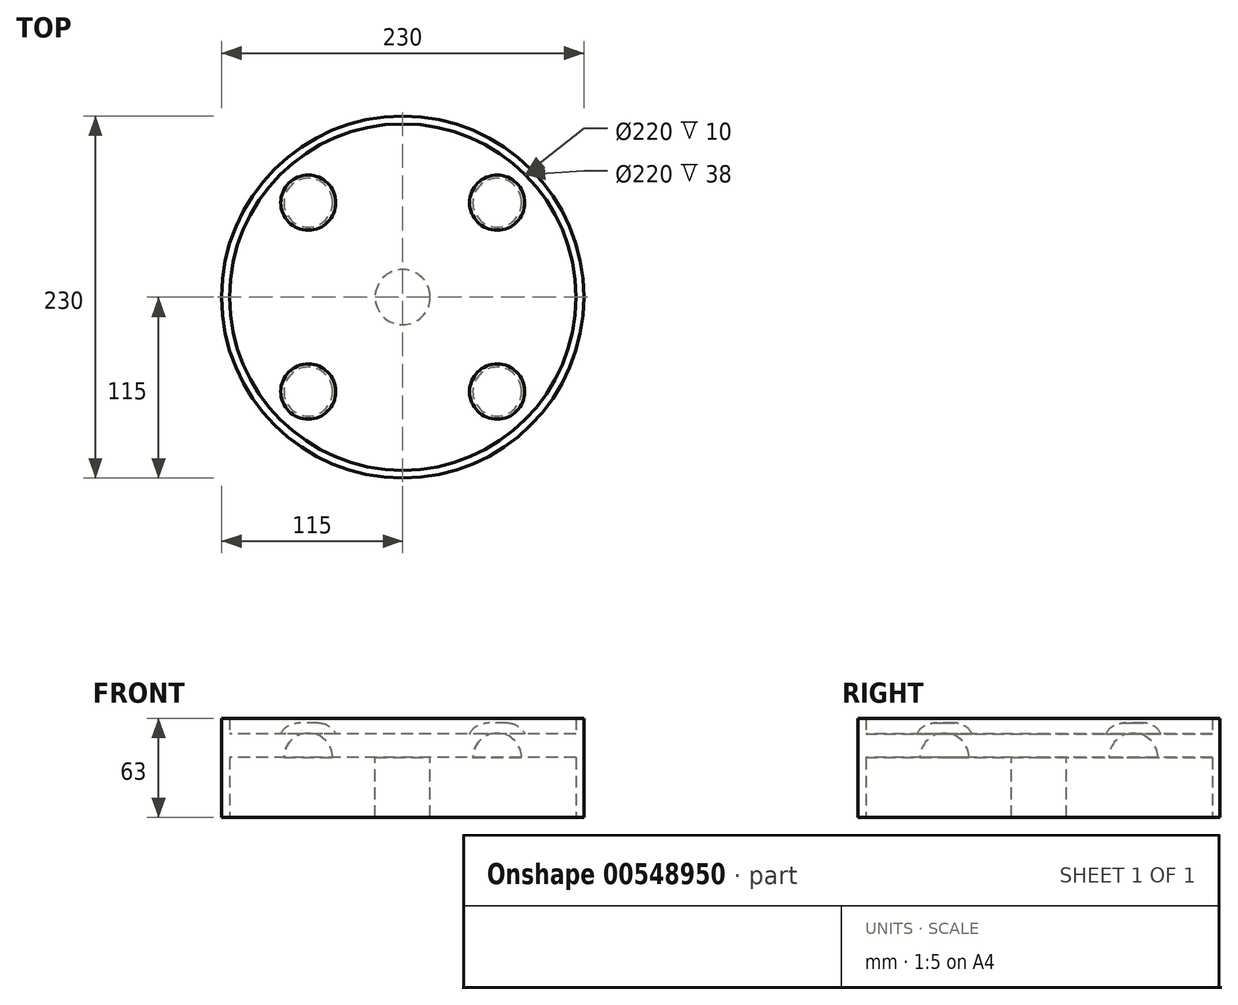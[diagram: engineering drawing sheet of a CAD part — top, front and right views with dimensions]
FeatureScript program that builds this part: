
annotation { "Feature Type Name" : "Feature", "Feature Type Description" : "" }
export const myFeature = defineFeature(function(context is Context, id is Id, definition is map)
    precondition{}
    {
        {
            var Q0;
            Q0=qCreatedBy(makeId("Top.planeOp"),FACE);
            var sketch = newSketch(context, id + "F0", { "sketchPlane" : qUnion([Q0])});
            skCircle(sketch, "E0", {"center": v(0, 0) * mm, "radius": 115 * mm});
            skSolve(sketch);
        }
        {
            var Q0;
            Q0 = qSketchRegion(id + "F0", true);
            extrude(context, id + "F1", {"entities" : qUnion([Q0]), "depth" : 15 * mm, "offsetDistance" : 25 * mm});
        }
        {
            var Q0;
            Q0=makeQuery(id+"F1.opExtrude","CAP_FACE",FACE,{"disambiguationData":[OSD([sQuery(id+"F0.wireOp",EDGE,"E0")])],"isStart":true});
            var sketch = newSketch(context, id + "F2", { "sketchPlane" : qUnion([Q0])});
            skCircle(sketch, "E1", {"center": v(0, 0) * mm, "radius": 17.5 * mm});
            skSolve(sketch);
        }
        {
            var Q0;
            Q0 = qSketchRegion(id + "F2", true);
            extrude(context, id + "F3", {"entities" : qUnion([Q0]), "operationType" : NewBodyOperationType.ADD, "depth" : 38 * mm, "offsetDistance" : 25 * mm});
        }
        {
            var Q0;
            Q0=makeQuery(id+"F1.opExtrude","CAP_FACE",FACE,{"disambiguationData":[OSD([sQuery(id+"F0.wireOp",EDGE,"E0")])],"isStart":false});
            var sketch = newSketch(context, id + "F4", { "sketchPlane" : qUnion([Q0])});
            skCircle(sketch, "E2", {"center": v(-60, 60) * mm, "radius": 17.5 * mm});
            skCircle(sketch, "E3.1.0", {"center": v(-60, -60) * mm, "radius": 17.5 * mm});
            skCircle(sketch, "E3.2.0", {"center": v(60, -60) * mm, "radius": 17.5 * mm});
            skCircle(sketch, "E3.3.0", {"center": v(60, 60) * mm, "radius": 17.5 * mm});
            skPoint(sketch, "E3.center", {"position": v(0, 0) * mm});
            skSolve(sketch);
        }
        {
            var Q0;
            Q0 = qSketchRegion(id + "F4", true);
            extrude(context, id + "F5", {"entities" : qUnion([Q0]), "operationType" : NewBodyOperationType.ADD, "depth" : 7 * mm, "offsetDistance" : 25 * mm});
        }
        {
            var Q0;
            Q0=makeQuery(id+"F1.opExtrude","CAP_FACE",FACE,{"disambiguationData":[OSD([sQuery(id+"F0.wireOp",EDGE,"E0")])],"isStart":true});
            var sketch = newSketch(context, id + "F6", { "sketchPlane" : qUnion([Q0])});
            skCircle(sketch, "E4", {"center": v(-60, 60) * mm, "radius": 15.5 * mm});
            skCircle(sketch, "E5.1.0", {"center": v(-60, -60) * mm, "radius": 15.5 * mm});
            skCircle(sketch, "E5.2.0", {"center": v(60, -60) * mm, "radius": 15.5 * mm});
            skCircle(sketch, "E5.3.0", {"center": v(60, 60) * mm, "radius": 15.5 * mm});
            skPoint(sketch, "E5.center", {"position": v(0, 0) * mm});
            skSolve(sketch);
        }
        {
            var Q0;
            Q0 = qSketchRegion(id + "F6", true);
            extrude(context, id + "F7", {"entities" : qUnion([Q0]), "operationType" : NewBodyOperationType.REMOVE, "oppositeDirection" : true, "depth" : 15.5 * mm, "offsetDistance" : 25 * mm});
        }
        {
            var Q0;
            Q0=makeQuery(id+"F7.boolean.opBoolean","COPY",EDGE,{"derivedFrom":makeQuery(id+"F7.opExtrude","CAP_EDGE",EDGE,{"disambiguationData":[OSD([sQuery(id+"F6.wireOp",EDGE,"E4")])],"isStart":false})});
            var Q1;
            Q1=makeQuery(id+"F7.boolean.opBoolean","COPY",EDGE,{"derivedFrom":makeQuery(id+"F7.opExtrude","CAP_EDGE",EDGE,{"disambiguationData":[OSD([sQuery(id+"F6.wireOp",EDGE,"E5.3.0")])],"isStart":false})});
            var Q2;
            Q2=makeQuery(id+"F7.boolean.opBoolean","COPY",EDGE,{"derivedFrom":makeQuery(id+"F7.opExtrude","CAP_EDGE",EDGE,{"disambiguationData":[OSD([sQuery(id+"F6.wireOp",EDGE,"E5.2.0")])],"isStart":false})});
            var Q3;
            Q3=makeQuery(id+"F7.boolean.opBoolean","COPY",EDGE,{"derivedFrom":makeQuery(id+"F7.opExtrude","CAP_EDGE",EDGE,{"disambiguationData":[OSD([sQuery(id+"F6.wireOp",EDGE,"E5.1.0")])],"isStart":false})});
            fillet(context, id + "F8", {"entities" : qUnion([Q0, Q1, Q2, Q3]), "radius" : 15.5 * mm, "tangentPropagation" : true, "allowEdgeOverflow" : false});
        }
        {
            var Q0;
            Q0=makeQuery(id+"F5.opExtrude","CAP_EDGE",EDGE,{"disambiguationData":[OSD([sQuery(id+"F4.wireOp",EDGE,"E3.1.0")])],"isStart":false});
            var Q1;
            Q1=makeQuery(id+"F5.opExtrude","CAP_EDGE",EDGE,{"disambiguationData":[OSD([sQuery(id+"F4.wireOp",EDGE,"E2")])],"isStart":false});
            var Q2;
            Q2=makeQuery(id+"F5.opExtrude","CAP_EDGE",EDGE,{"disambiguationData":[OSD([sQuery(id+"F4.wireOp",EDGE,"E3.3.0")])],"isStart":false});
            var Q3;
            Q3=makeQuery(id+"F5.opExtrude","CAP_EDGE",EDGE,{"disambiguationData":[OSD([sQuery(id+"F4.wireOp",EDGE,"E3.2.0")])],"isStart":false});
            fillet(context, id + "F9", {"entities" : qUnion([Q0, Q1, Q2, Q3]), "radius" : 12 * mm, "tangentPropagation" : true, "allowEdgeOverflow" : false});
        }
        {
            var Q0;
            Q0=makeQuery(id+"F1.opExtrude","CAP_FACE",FACE,{"disambiguationData":[OSD([sQuery(id+"F0.wireOp",EDGE,"E0")])],"isStart":false});
            var sketch = newSketch(context, id + "F10", { "sketchPlane" : qUnion([Q0])});
            skCircle(sketch, "E6", {"center": v(0, 0) * mm, "radius": 115 * mm});
            skCircle(sketch, "E7", {"center": v(0, 0) * mm, "radius": 110 * mm});
            skSolve(sketch);
        }
        {
            var Q0;
            Q0 = qSketchRegion(id + "F10", true);
            extrude(context, id + "F11", {"entities" : qUnion([Q0]), "operationType" : NewBodyOperationType.ADD, "depth" : 10 * mm, "offsetDistance" : 25 * mm, "hasSecondDirection" : true, "secondDirectionOppositeDirection" : true, "secondDirectionDepth" : 53 * mm});
        }
    });
